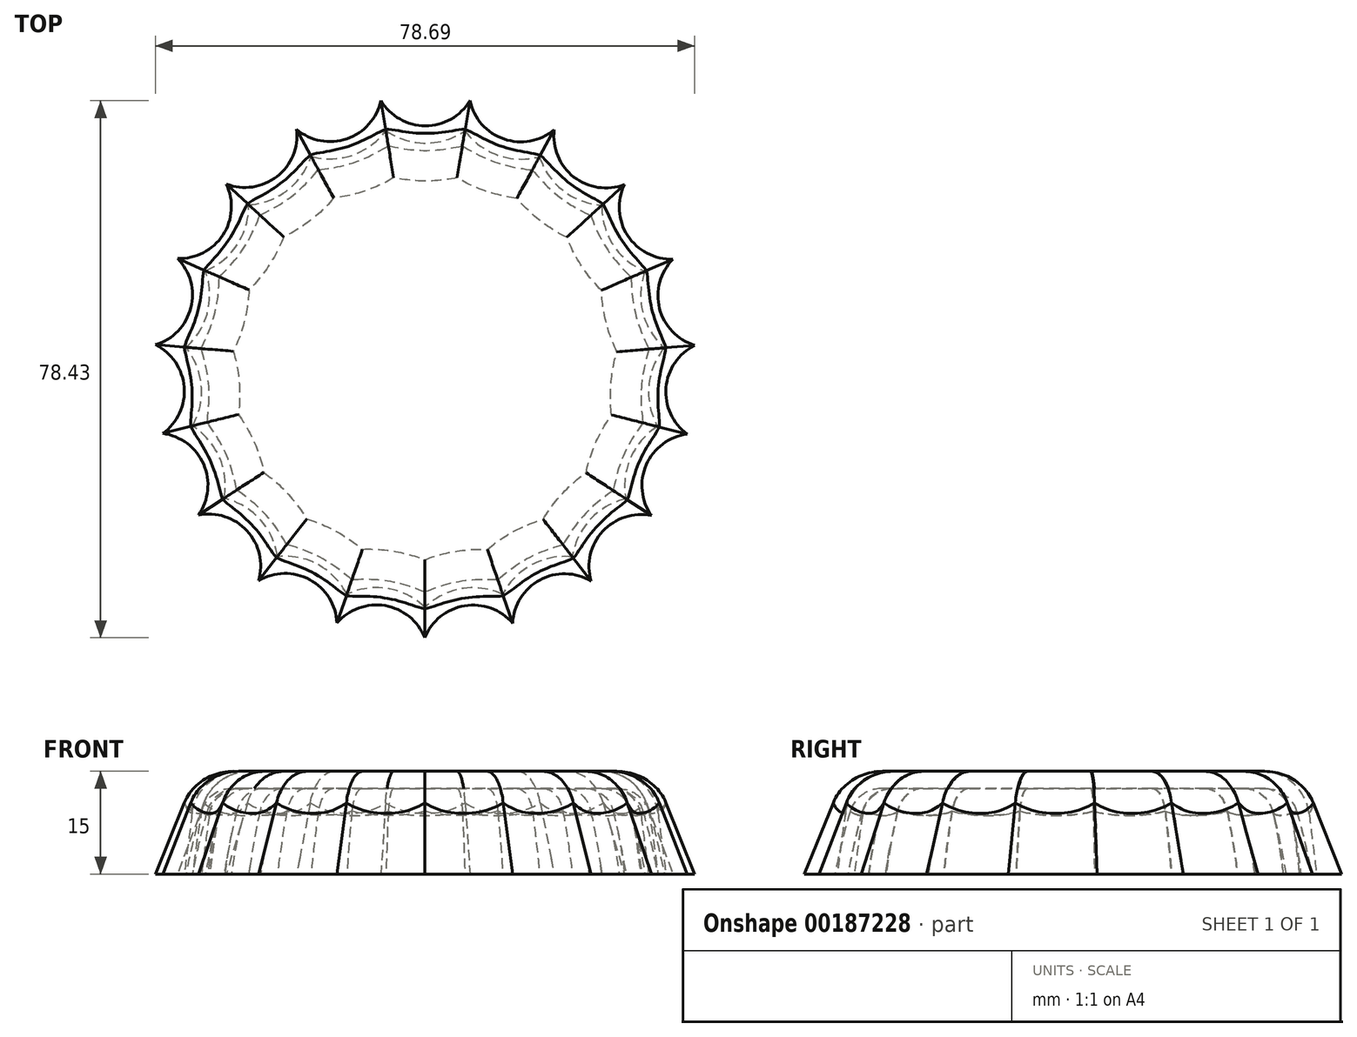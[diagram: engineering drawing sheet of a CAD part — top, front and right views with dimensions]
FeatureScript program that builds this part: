
annotation { "Feature Type Name" : "Feature", "Feature Type Description" : "" }
export const myFeature = defineFeature(function(context is Context, id is Id, definition is map)
    precondition{}
    {
        {
            var Q0;
            Q0=qCreatedBy(makeId("Top.planeOp"),FACE);
            var sketch = newSketch(context, id + "F0", { "sketchPlane" : qUnion([Q0])});
            skCircle(sketch, "E0", {"center": v(0, 0) * mm, "radius": 35.38 * mm, "construction": true});
            skCircle(sketch, "E1", {"center": v(0, 0) * mm, "radius": 40.27 * mm, "construction": true});
            skArc(sketch, "E2", {"start": v(-6.84, 39.68) * mm, "mid": v(0.04, 35.28) * mm, "end": v(6.94, 39.67) * mm});
            skArc(sketch, "E3.1.0", {"start": v(-19.35, 35.31) * mm, "mid": v(-11.41, 33.38) * mm, "end": v(-6.32, 39.77) * mm});
            skArc(sketch, "E3.2.0", {"start": v(-29.77, 27.12) * mm, "mid": v(-21.63, 27.87) * mm, "end": v(-18.89, 35.56) * mm});
            skArc(sketch, "E3.3.0", {"start": v(-36.96, 15.98) * mm, "mid": v(-29.51, 19.33) * mm, "end": v(-29.41, 27.5) * mm});
            skArc(sketch, "E3.4.0", {"start": v(-40.15, 3.11) * mm, "mid": v(-34.19, 8.7) * mm, "end": v(-36.75, 16.46) * mm});
            skArc(sketch, "E3.5.0", {"start": v(-38.98, -10.1) * mm, "mid": v(-35.16, -2.87) * mm, "end": v(-40.1, 3.64) * mm});
            skArc(sketch, "E3.6.0", {"start": v(-33.6, -22.2) * mm, "mid": v(-32.32, -14.13) * mm, "end": v(-39.11, -9.58) * mm});
            skArc(sketch, "E3.7.0", {"start": v(-24.56, -31.9) * mm, "mid": v(-25.98, -23.86) * mm, "end": v(-33.88, -21.76) * mm});
            skArc(sketch, "E3.8.0", {"start": v(-12.87, -38.15) * mm, "mid": v(-16.83, -31) * mm, "end": v(-24.98, -31.58) * mm});
            skArc(sketch, "E3.9.0", {"start": v(0.21, -40.27) * mm, "mid": v(-5.85, -34.8) * mm, "end": v(-13.37, -37.98) * mm});
            skArc(sketch, "E3.10.0", {"start": v(13.28, -38.02) * mm, "mid": v(5.76, -34.8) * mm, "end": v(-0.31, -40.27) * mm});
            skArc(sketch, "E3.11.0", {"start": v(24.9, -31.65) * mm, "mid": v(16.75, -31.05) * mm, "end": v(12.78, -38.19) * mm});
            skArc(sketch, "E3.12.0", {"start": v(33.83, -21.85) * mm, "mid": v(25.93, -23.93) * mm, "end": v(24.49, -31.97) * mm});
            skArc(sketch, "E4.2.13.0", {"start": v(39.09, -9.68) * mm, "mid": v(32.29, -14.21) * mm, "end": v(33.54, -22.29) * mm});
            skArc(sketch, "E5.2.14.0", {"start": v(40.11, 3.54) * mm, "mid": v(35.15, -2.96) * mm, "end": v(38.96, -10.19) * mm});
            skArc(sketch, "E6.2.15.0", {"start": v(36.8, 16.37) * mm, "mid": v(34.2, 8.62) * mm, "end": v(40.16, 3.01) * mm});
            skArc(sketch, "E7.2.16.0", {"start": v(29.48, 27.43) * mm, "mid": v(29.56, 19.26) * mm, "end": v(37, 15.89) * mm});
            skArc(sketch, "E8.2.17.0", {"start": v(18.98, 35.52) * mm, "mid": v(21.7, 27.81) * mm, "end": v(29.84, 27.04) * mm});
            skArc(sketch, "E9.2.18.0", {"start": v(6.42, 39.75) * mm, "mid": v(11.5, 33.35) * mm, "end": v(19.44, 35.26) * mm});
            skSolve(sketch);
        }
        {
            var Q0;
            Q0=qCreatedBy(makeId("Top.planeOp"),FACE);
            cPlane(context, id + "F1", {"entities" : qUnion([Q0]), "cplaneType" : CPlaneType.OFFSET, "offset" : 15 * mm, "width" : 150 * mm, "height" : 150 * mm});
        }
        {
            var Q0;
            Q0=qCreatedBy(id+"F1.planeOp",FACE);
            var sketch = newSketch(context, id + "F2", { "sketchPlane" : qUnion([Q0])});
            skCircle(sketch, "E10", {"center": v(0, 0) * mm, "radius": 33.4 * mm});
            skSolve(sketch);
        }
        {
            var Q0;
            Q0 = qSketchRegion(id + "F2", true);
            var Q1;
            Q1 = qSketchRegion(id + "F0", true);
            loft(context, id + "F3", {"sheetProfilesArray" : [{ "sheetProfileEntities" : qUnion([Q0]) }, { "sheetProfileEntities" : qUnion([Q1]) }]});
        }
        {
            var Q0;
            Q0=makeQuery(id+"F3.opLoft","CAP_FACE",FACE,{"disambiguationData":[OSD([makeQuery(id+"F2.imprint","IMPRINT",FACE,{"disambiguationData":[TD([[makeQuery(id+"F2.imprint","IMPRINT",EDGE,{"derivedFrom":sQuery(id+"F2.wireOp",EDGE,"E10")}),1.0]])]})])],"isStart":true});
            fillet(context, id + "F4", {"entities" : qUnion([Q0]), "radius" : 7 * mm, "tangentPropagation" : true, "allowEdgeOverflow" : false});
        }
        {
            var Q0;
            {var subQ5=sQuery(id+"F0.wireOp",EDGE,"E3.1.0");var subQ6=sQuery(id+"F0.wireOp",EDGE,"E2");var subQ7=makeQuery(id+"F0.imprint","INTERSECT",VERTEX,{"derivedFrom":[subQ6,subQ5]});Q0=makeQuery(id+"F3.opLoft","CAP_FACE",FACE,{"disambiguationData":[OSD([makeQuery(id+"F0.imprint","IMPRINT",FACE,{"disambiguationData":[TD([[makeQuery(id+"F0.imprint","IMPRINT",EDGE,{"disambiguationData":[TD([[subQ7,-1.0]])],"derivedFrom":subQ6}),-1.0]])]})])],"isStart":true});}
            shell(context, id + "F5", {"entities" : qUnion([Q0]), "thickness" : 2.5 * mm});
        }
    });
